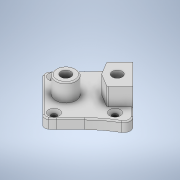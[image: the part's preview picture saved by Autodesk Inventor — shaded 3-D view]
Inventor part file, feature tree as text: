
AUTODESK INVENTOR PART (.ipt)
format: ipt  version: 2020.3 (Build 243373000, 373)  size: 396,800 bytes
history: native  units: mm
features: sketch x4, extrude x4, hole x4, fillet x2, projected_geometry x1
ambient origin geometry x8: Origin, YZ Plane, XZ Plane, XY Plane, X Axis, Y Axis, Z Axis, Center Point
bodies: Body1 (feature_tree)
feature tree (15):
  sketch  "Sketch1"  dims[d0=135.0deg d4=24.6mm]
  extrude  "Extrusion12"  Depth=24.6mm
  extrude  "Extrusion13"  Depth=12.4mm
  extrude  "Extrusion14"  Depth=8.5mm
  extrude  "Extrusion15"  Depth=6.0mm
  sketch  "Sketch3"  dims[d7=60.0mm d9=8.5mm]
  fillet  "Fillet10"  Radius=2.0mm
  fillet  "Fillet11"  Radius=2.0mm
  hole  "Hole3"  [1 undecoded]
  hole  "Hole5"  [1 undecoded]
  hole  "Hole6"  [1 undecoded]
  hole  "Hole7"  [1 undecoded]
  sketch  "Sketch2"  dims[d5=12.4mm d6=70.0mm]
  projected_geometry  "Projected Loop1"
  sketch  "Sketch5"  dims[d10=135.0deg d12=6.0mm d13=2.0mm d14=2.0mm d16=20.0mm d23=6.0mm d29=130.0mm d32=15.0mm d33=4.0mm d34=28.4mm d38=4.0mm d40=6.8mm d49=30.0mm d50=84.0mm d51=3.0mm d52=3.0mm d53=1.5mm d54=20.0mm d59=1.0mm d60=90.0mm d61=135.0deg d70=135.0deg d82=0.7mm d83=0.7mm d84=0.7mm d85=0.7mm d86=6.0mm d102=4.0mm d103=0.0mm d104=4.0mm d105=0.0mm d106=11.4mm d107=0.0mm d108=18.0mm d116=2.0mm d117=0.5mm d118=4.2mm d119=6.0mm d120=7.2mm d121=1.6mm d122=90.0deg d123=5.0mm d124=0.0mm d125=11.4mm d126=0.0mm d134=5.7mm d135=7.2mm d136=4.2mm d137=6.0mm d138=5.6mm d139=0.85mm d140=90.0deg d141=8.0mm d142=0.0mm d143=5.6mm d152=5.6mm d153=6.0mm d154=9.0mm d155=1.0mm d156=90.0deg d157=6.5mm d158=0.0mm d159=2.3mm d160=6.0mm d161=4.5mm d162=0.8mm d163=90.0deg d164=6.5mm d165=0.0mm d166=2.0mm d167=2.0mm d127=0.0625mm d128=0.75mm d129=0.375mm]
note: 4 required parameter values undecoded (feature->parameter linkage not recoverable at this tier; creation-order binding heuristic only, values carry confidence <= 0.55)
